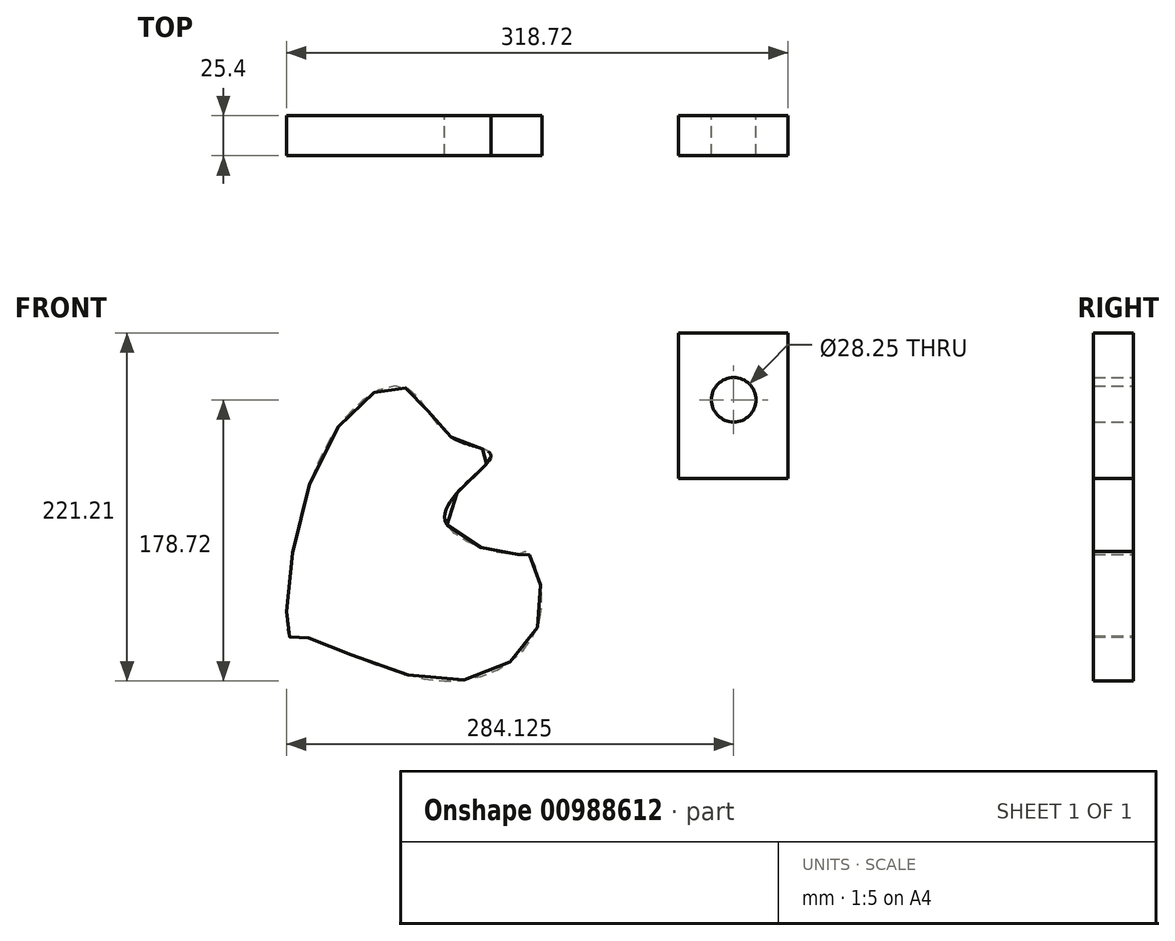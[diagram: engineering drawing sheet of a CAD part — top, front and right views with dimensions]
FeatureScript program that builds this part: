
annotation { "Feature Type Name" : "Feature", "Feature Type Description" : "" }
export const myFeature = defineFeature(function(context is Context, id is Id, definition is map)
    precondition{}
    {
        {
            var Q0;
            Q0=qCreatedBy(makeId("Front.planeOp"),FACE);
            var sketch = newSketch(context, id + "F0", { "sketchPlane" : qUnion([Q0])});
            skFitSpline(sketch, "E0", {"points": [v(-111.68, 17.73) * mm, v(-140.65, 49.06) * mm, v(-194.24, 6.07) * mm, v(-214.81, -108.8) * mm, v(-209.02, -108.57) * mm, v(-115.74, -137.27) * mm, v(-54.9, -95.95) * mm, v(-63.59, -55.3) * mm, v(-69.67, -56.76) * mm, v(-115.74, -33.84) * mm, v(-86.48, 5.6) * mm, v(-111.68, 17.73) * mm]});
            skSolve(sketch);
        }
        {
            var Q0;
            Q0 = qSketchRegion(id + "F0", true);
            extrude(context, id + "F1", {"entities" : qUnion([Q0]), "depth" : 25.4 * mm, "offsetDistance" : 25.4 * mm});
        }
        {
            var Q0;
            Q0=qCreatedBy(makeId("Front.planeOp"),FACE);
            var sketch = newSketch(context, id + "F2", { "sketchPlane" : qUnion([Q0])});
            skLineSegment(sketch, "E1.bottom", {"start": v(32.7, 83.9) * mm, "end": v(102.37, 83.9) * mm});
            skLineSegment(sketch, "E1.top", {"start": v(32.7, -8.53) * mm, "end": v(102.37, -8.53) * mm});
            skLineSegment(sketch, "E1.left", {"start": v(32.7, 83.9) * mm, "end": v(32.7, -8.53) * mm});
            skLineSegment(sketch, "E1.right", {"start": v(102.37, 83.9) * mm, "end": v(102.37, -8.53) * mm});
            skCircle(sketch, "E2", {"center": v(67.77, 41.41) * mm, "radius": 14.13 * mm});
            skSolve(sketch);
        }
        {
            var Q0;
            Q0 = qSketchRegion(id + "F2", true);
            extrude(context, id + "F3", {"entities" : qUnion([Q0]), "depth" : 25.4 * mm, "offsetDistance" : 25.4 * mm});
        }
    });
